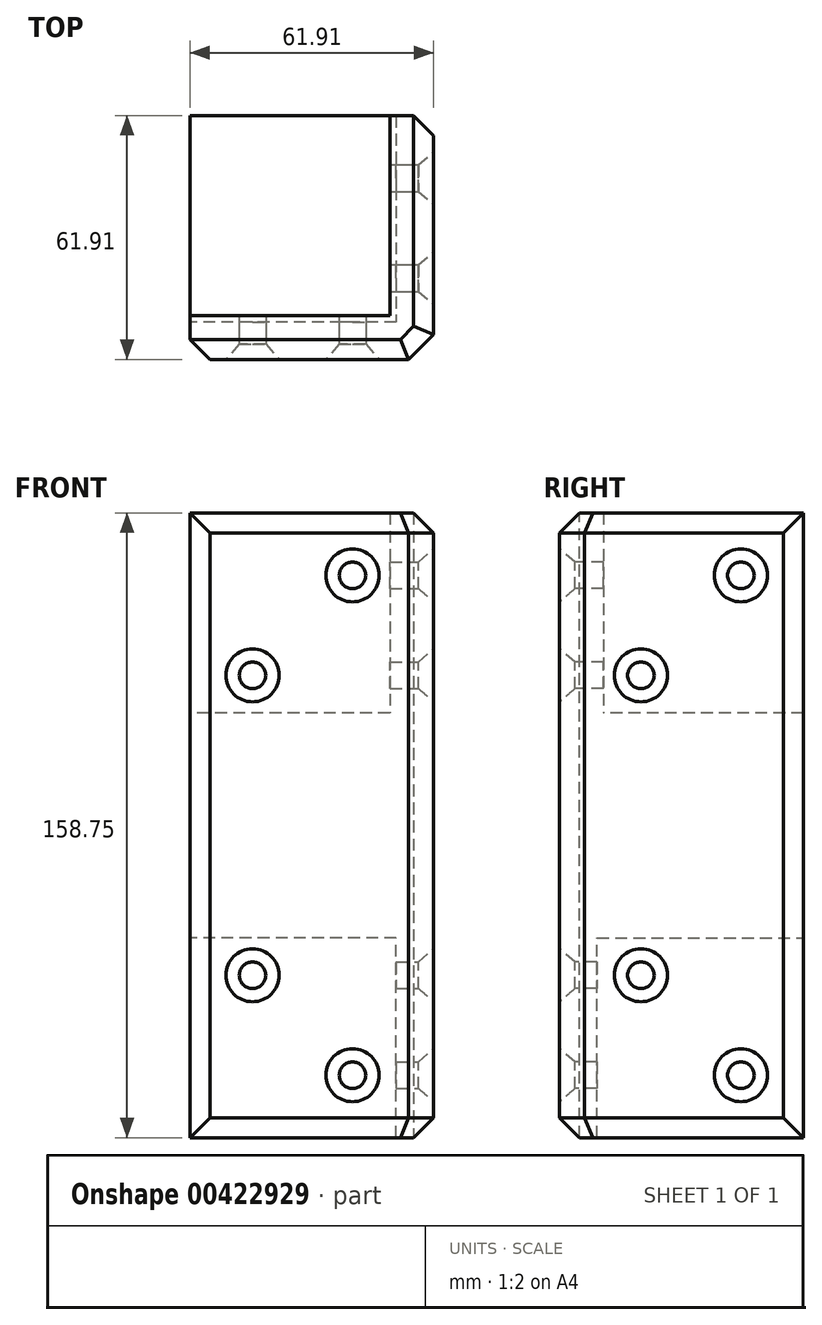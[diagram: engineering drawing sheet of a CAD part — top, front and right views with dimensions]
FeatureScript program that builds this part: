
annotation { "Feature Type Name" : "Feature", "Feature Type Description" : "" }
export const myFeature = defineFeature(function(context is Context, id is Id, definition is map)
    precondition{}
    {
        {
            var Q0;
            Q0=qCreatedBy(makeId("Top.planeOp"),FACE);
            var sketch = newSketch(context, id + "F0", { "sketchPlane" : qUnion([Q0])});
            skLineSegment(sketch, "E0", {"start": v(0, 0) * mm, "end": v(0, 61.91) * mm});
            skLineSegment(sketch, "E1", {"start": v(0, 61.91) * mm, "end": v(-11.11, 61.91) * mm});
            skLineSegment(sketch, "E2", {"start": v(-11.11, 61.91) * mm, "end": v(-11.11, 11.11) * mm});
            skLineSegment(sketch, "E3", {"start": v(-11.11, 11.11) * mm, "end": v(-61.91, 11.11) * mm});
            skLineSegment(sketch, "E4", {"start": v(-61.91, 11.11) * mm, "end": v(-61.91, 0) * mm});
            skLineSegment(sketch, "E5", {"start": v(-61.91, 0) * mm, "end": v(0, 0) * mm});
            skSolve(sketch);
        }
        {
            var Q0;
            Q0=makeQuery(id+"F0.imprint","IMPRINT",FACE,{"disambiguationData":[TD([[makeQuery(id+"F0.imprint","IMPRINT",EDGE,{"derivedFrom":sQuery(id+"F0.wireOp",EDGE,"E0")}),1.0]])]});
            extrude(context, id + "F1", {"entities" : qUnion([Q0]), "depth" : 50.8 * mm});
        }
        {
            var Q0;
            Q0=qCreatedBy(makeId("Top.planeOp"),FACE);
            var sketch = newSketch(context, id + "F2", { "sketchPlane" : qUnion([Q0])});
            skLineSegment(sketch, "E6.bottom", {"start": v(0, 0) * mm, "end": v(-61.91, 0) * mm});
            skLineSegment(sketch, "E6.top", {"start": v(0, 61.91) * mm, "end": v(-61.91, 61.91) * mm});
            skLineSegment(sketch, "E6.left", {"start": v(0, 0) * mm, "end": v(0, 61.91) * mm});
            skLineSegment(sketch, "E6.right", {"start": v(-61.91, 0) * mm, "end": v(-61.91, 61.91) * mm});
            skSolve(sketch);
        }
        {
            var Q0;
            Q0 = qSketchRegion(id + "F2", true);
            extrude(context, id + "F3", {"entities" : qUnion([Q0]), "operationType" : NewBodyOperationType.ADD, "oppositeDirection" : true, "depth" : 57.15 * mm});
        }
        {
            var Q0;
            Q0=makeQuery(id+"F3.opExtrude","CAP_FACE",FACE,{"disambiguationData":[OSD([sQuery(id+"F2.wireOp",EDGE,"E6.bottom"),sQuery(id+"F2.wireOp",EDGE,"E6.top"),sQuery(id+"F2.wireOp",EDGE,"E6.left"),sQuery(id+"F2.wireOp",EDGE,"E6.right")])],"isStart":false});
            var sketch = newSketch(context, id + "F4", { "sketchPlane" : qUnion([Q0])});
            skLineSegment(sketch, "E7", {"start": v(0, 0) * mm, "end": v(0, -61.91) * mm});
            skLineSegment(sketch, "E8", {"start": v(0, -61.91) * mm, "end": v(-9.52, -61.91) * mm});
            skLineSegment(sketch, "E9", {"start": v(-9.52, -61.91) * mm, "end": v(-9.52, -9.52) * mm});
            skLineSegment(sketch, "E10", {"start": v(-9.52, -9.52) * mm, "end": v(-61.91, -9.53) * mm});
            skLineSegment(sketch, "E11", {"start": v(-61.91, -9.53) * mm, "end": v(-61.91, 0) * mm});
            skLineSegment(sketch, "E12", {"start": v(-61.91, 0) * mm, "end": v(0, 0) * mm});
            skSolve(sketch);
        }
        {
            var Q0;
            Q0 = qSketchRegion(id + "F4", true);
            extrude(context, id + "F5", {"entities" : qUnion([Q0]), "operationType" : NewBodyOperationType.ADD, "depth" : 50.8 * mm});
        }
        {
            var Q0;
            Q0=makeQuery(id+"F1.opExtrude","SWEPT_FACE",FACE,{"disambiguationData":[OSD([sQuery(id+"F0.wireOp",EDGE,"E0")])]});
            var sketch = newSketch(context, id + "F6", { "sketchPlane" : qUnion([Q0])});
            skCircle(sketch, "E13", {"center": v(46.04, 34.93) * mm, "radius": 3.18 * mm});
            skCircle(sketch, "E14", {"center": v(20.64, 9.53) * mm, "radius": 3.18 * mm});
            skLineSegment(sketch, "E15", {"start": v(61.91, -28.57) * mm, "end": v(0, -28.57) * mm, "construction": true});
            skCircle(sketch, "E16.MirrorC", {"center": v(46.04, -92.07) * mm, "radius": 3.18 * mm});
            skCircle(sketch, "E17.MirrorC", {"center": v(20.64, -66.67) * mm, "radius": 3.18 * mm});
            skLineSegment(sketch, "E18", {"start": v(61.91, -28.57) * mm, "end": v(61.91, 61.23) * mm, "construction": true});
            skSolve(sketch);
        }
        {
            var Q0;
            Q0=makeQuery(id+"F1.opExtrude","SWEPT_FACE",FACE,{"disambiguationData":[OSD([sQuery(id+"F0.wireOp",EDGE,"E5")])]});
            var sketch = newSketch(context, id + "F7", { "sketchPlane" : qUnion([Q0])});
            skCircle(sketch, "E19", {"center": v(-20.64, 34.93) * mm, "radius": 3.18 * mm});
            skCircle(sketch, "E20", {"center": v(-46.04, 9.53) * mm, "radius": 3.18 * mm});
            skLineSegment(sketch, "E21", {"start": v(-61.91, -28.57) * mm, "end": v(0, -28.57) * mm, "construction": true});
            skCircle(sketch, "E22.MirrorC", {"center": v(-20.64, -92.07) * mm, "radius": 3.18 * mm});
            skCircle(sketch, "E23.MirrorC", {"center": v(-46.04, -66.67) * mm, "radius": 3.18 * mm});
            skLineSegment(sketch, "E24", {"start": v(-61.91, -28.57) * mm, "end": v(-61.91, 64) * mm, "construction": true});
            skSolve(sketch);
        }
        {
            var Q0;
            Q0=sQuery(id+"F6.wireOp",VERTEX,"E13.center");
            var Q1;
            Q1=sQuery(id+"F6.wireOp",VERTEX,"E14.center");
            var Q2;
            Q2=sQuery(id+"F6.wireOp",VERTEX,"a73e6468-ef55-433b-9e5c-053ff8b837081.MirrorC.center");
            var Q3;
            Q3=sQuery(id+"F6.wireOp",VERTEX,"a73e6468-ef55-433b-9e5c-053ff8b837080.MirrorC.center");
            var Q4;
            Q4=sQuery(id+"F6.wireOp",VERTEX,"E17.MirrorC.center");
            var Q5;
            Q5=sQuery(id+"F6.wireOp",VERTEX,"E16.MirrorC.center");
            var Q6;
            Q6=sQuery(id+"F7.wireOp",VERTEX,"E19.center");
            var Q7;
            Q7=sQuery(id+"F7.wireOp",VERTEX,"E20.center");
            var Q8;
            Q8=sQuery(id+"F7.wireOp",VERTEX,"E23.MirrorC.center");
            var Q9;
            Q9=sQuery(id+"F7.wireOp",VERTEX,"E22.MirrorC.center");
            var Q10;
            Q10=makeQuery(id+"F1.opExtrude","SWEPT_BODY",BODY,{"disambiguationData":[OSD([sQuery(id+"F0.wireOp",EDGE,"E0"),sQuery(id+"F0.wireOp",EDGE,"E1"),sQuery(id+"F0.wireOp",EDGE,"E2"),sQuery(id+"F0.wireOp",EDGE,"E3"),sQuery(id+"F0.wireOp",EDGE,"E4"),sQuery(id+"F0.wireOp",EDGE,"E5")])]});
            hole(context, id + "F8", {"style" : HoleStyle.C_SINK, "endStyle" : HoleEndStyle.THROUGH, "standardTappedOrClearance" : lookupTablePath({ "standard" : "ANSI", "fit" : "Normal (ASME)", "size" : "1/4", "type" : "Clearance" }), "standardBlindInLast" : lookupTablePath({ "fit" : "Free", "standard" : "ANSI", "size" : "1/4", "type" : "Clearance" }), "holeDiameter" : 6.76 * mm, "cSinkDiameter" : 13.5 * mm, "cSinkAngle" : 82 * degree, "isTappedThrough" : true, "tappedDepth" : 12.7 * mm, "tapClearance" : 3, "locations" : qUnion([Q0, Q1, Q2, Q3, Q4, Q5, Q6, Q7, Q8, Q9]), "scope" : qUnion([Q10])});
        }
        {
            var Q0;
            Q0=makeQuery(id+"F1.opExtrude","SWEPT_EDGE",EDGE,{"disambiguationData":[OSD([sQuery(id+"F0.wireOp",EDGE,"E0"),sQuery(id+"F0.wireOp",EDGE,"E5")])]});
            chamfer(context, id + "F9", {"entities" : qUnion([Q0]), "width" : 6.35 * mm, "tangentPropagation" : true});
        }
        {
            var Q0;
            Q0=makeQuery(id+"F1.opExtrude","SWEPT_EDGE",EDGE,{"disambiguationData":[OSD([sQuery(id+"F0.wireOp",EDGE,"E4"),sQuery(id+"F0.wireOp",EDGE,"E5")])]});
            var Q1;
            Q1=makeQuery(id+"F1.opExtrude","SWEPT_EDGE",EDGE,{"disambiguationData":[OSD([sQuery(id+"F0.wireOp",EDGE,"E0"),sQuery(id+"F0.wireOp",EDGE,"E1")])]});
            chamfer(context, id + "F10", {"entities" : qUnion([Q0, Q1]), "width" : 5.08 * mm, "tangentPropagation" : true});
        }
        {
            var Q0;
            Q0=makeQuery(id+"F1.opExtrude","CAP_EDGE",EDGE,{"disambiguationData":[OSD([sQuery(id+"F0.wireOp",EDGE,"E5")])],"isStart":false});
            var Q1;
            {var subQ0=sQuery(id+"F0.wireOp",EDGE,"E5");var subQ1=sQuery(id+"F0.wireOp",EDGE,"E0");Q1=makeQuery(id+"F9.opChamfer","BLEND_EDGE",EDGE,{"blendedFrom":[makeQuery(id+"F5.boolean.opBoolean","MERGE",EDGE,{"derivedFrom":[makeQuery(id+"F3.boolean.opBoolean","MERGE",EDGE,{"derivedFrom":[makeQuery(id+"F1.opExtrude","SWEPT_EDGE",EDGE,{"disambiguationData":[OSD([subQ1,subQ0])]}),makeQuery(id+"F3.opExtrude","SWEPT_EDGE",EDGE,{"disambiguationData":[OSD([sQuery(id+"F2.wireOp",EDGE,"E6.bottom"),sQuery(id+"F2.wireOp",EDGE,"E6.left")])]})]}),makeQuery(id+"F5.opExtrude","SWEPT_EDGE",EDGE,{"disambiguationData":[OSD([sQuery(id+"F4.wireOp",EDGE,"E7"),sQuery(id+"F4.wireOp",EDGE,"E12")])]})]}),makeQuery(id+"F1.opExtrude","CAP_FACE",FACE,{"disambiguationData":[OSD([subQ1,sQuery(id+"F0.wireOp",EDGE,"E1"),sQuery(id+"F0.wireOp",EDGE,"E2"),sQuery(id+"F0.wireOp",EDGE,"E3"),sQuery(id+"F0.wireOp",EDGE,"E4"),subQ0])],"isStart":false})],"blendedInto":[makeQuery(id+"F1.opExtrude","CAP_FACE",FACE,{"disambiguationData":[OSD([subQ1,sQuery(id+"F0.wireOp",EDGE,"E1"),sQuery(id+"F0.wireOp",EDGE,"E2"),sQuery(id+"F0.wireOp",EDGE,"E3"),sQuery(id+"F0.wireOp",EDGE,"E4"),subQ0])],"isStart":false})]});}
            var Q2;
            Q2=makeQuery(id+"F1.opExtrude","CAP_EDGE",EDGE,{"disambiguationData":[OSD([sQuery(id+"F0.wireOp",EDGE,"E0")])],"isStart":false});
            var Q3;
            {var subQ0=sQuery(id+"F4.wireOp",EDGE,"E12");var subQ1=sQuery(id+"F4.wireOp",EDGE,"E7");Q3=makeQuery(id+"F9.opChamfer","BLEND_EDGE",EDGE,{"blendedFrom":[makeQuery(id+"F5.boolean.opBoolean","MERGE",EDGE,{"derivedFrom":[makeQuery(id+"F3.boolean.opBoolean","MERGE",EDGE,{"derivedFrom":[makeQuery(id+"F1.opExtrude","SWEPT_EDGE",EDGE,{"disambiguationData":[OSD([sQuery(id+"F0.wireOp",EDGE,"E0"),sQuery(id+"F0.wireOp",EDGE,"E5")])]}),makeQuery(id+"F3.opExtrude","SWEPT_EDGE",EDGE,{"disambiguationData":[OSD([sQuery(id+"F2.wireOp",EDGE,"E6.bottom"),sQuery(id+"F2.wireOp",EDGE,"E6.left")])]})]}),makeQuery(id+"F5.opExtrude","SWEPT_EDGE",EDGE,{"disambiguationData":[OSD([subQ1,subQ0])]})]}),makeQuery(id+"F5.opExtrude","CAP_FACE",FACE,{"disambiguationData":[OSD([subQ1,sQuery(id+"F4.wireOp",EDGE,"E8"),sQuery(id+"F4.wireOp",EDGE,"E9"),sQuery(id+"F4.wireOp",EDGE,"E10"),sQuery(id+"F4.wireOp",EDGE,"E11"),subQ0])],"isStart":false})],"blendedInto":[makeQuery(id+"F5.opExtrude","CAP_FACE",FACE,{"disambiguationData":[OSD([subQ1,sQuery(id+"F4.wireOp",EDGE,"E8"),sQuery(id+"F4.wireOp",EDGE,"E9"),sQuery(id+"F4.wireOp",EDGE,"E10"),sQuery(id+"F4.wireOp",EDGE,"E11"),subQ0])],"isStart":false})]});}
            var Q4;
            Q4=makeQuery(id+"F5.opExtrude","CAP_EDGE",EDGE,{"disambiguationData":[OSD([sQuery(id+"F4.wireOp",EDGE,"E12")])],"isStart":false});
            var Q5;
            Q5=makeQuery(id+"F5.opExtrude","CAP_EDGE",EDGE,{"disambiguationData":[OSD([sQuery(id+"F4.wireOp",EDGE,"E7")])],"isStart":false});
            chamfer(context, id + "F11", {"entities" : qUnion([Q0, Q1, Q2, Q3, Q4, Q5]), "width" : 5.08 * mm, "tangentPropagation" : true});
        }
    });
